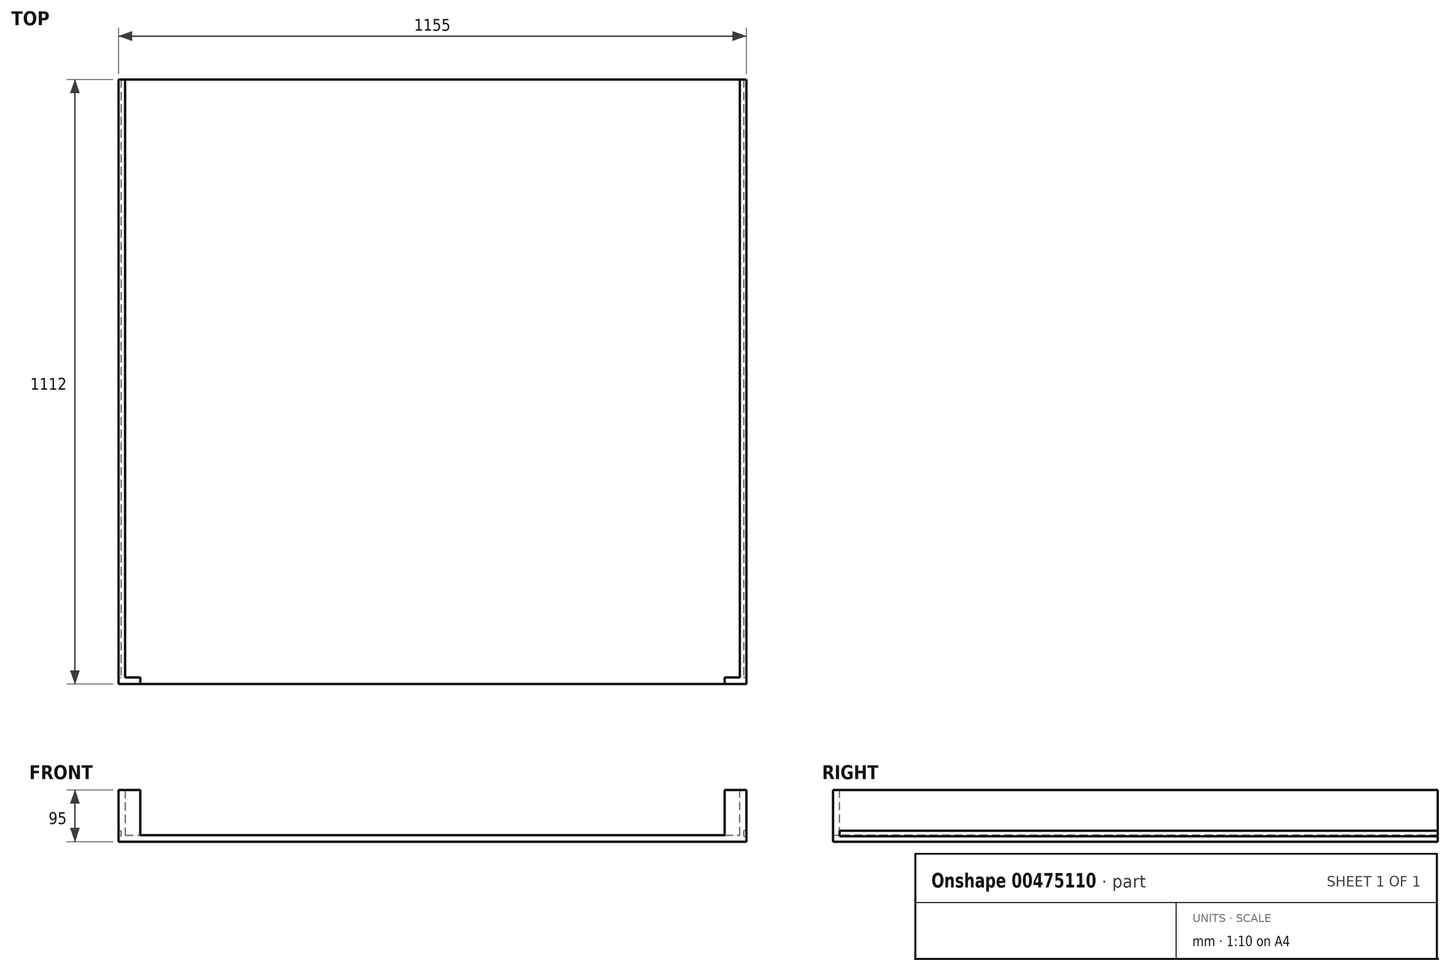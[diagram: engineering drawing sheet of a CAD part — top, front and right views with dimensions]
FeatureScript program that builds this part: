
annotation { "Feature Type Name" : "Feature", "Feature Type Description" : "" }
export const myFeature = defineFeature(function(context is Context, id is Id, definition is map)
    precondition{}
    {
        {
            var Q0;
            Q0=qCreatedBy(makeId("Front.planeOp"),FACE);
            var sketch = newSketch(context, id + "F0", { "sketchPlane" : qUnion([Q0])});
            skLineSegment(sketch, "E0.bottom", {"start": v(-577.5, 95) * mm, "end": v(577.5, 95) * mm, "construction": true});
            skLineSegment(sketch, "E0.top", {"start": v(-577.5, 0) * mm, "end": v(577.5, 0) * mm, "construction": true});
            skLineSegment(sketch, "E0.left", {"start": v(-577.5, 95) * mm, "end": v(-577.5, 0) * mm, "construction": true});
            skLineSegment(sketch, "E0.right", {"start": v(577.5, 95) * mm, "end": v(577.5, 0) * mm, "construction": true});
            skLineSegment(sketch, "E1", {"start": v(-577.5, 12) * mm, "end": v(577.5, 12) * mm, "construction": true});
            skLineSegment(sketch, "E2", {"start": v(-572.5, 95) * mm, "end": v(-572.5, 0) * mm, "construction": true});
            skLineSegment(sketch, "E3", {"start": v(572.5, 95) * mm, "end": v(572.5, 0) * mm, "construction": true});
            skLineSegment(sketch, "E4", {"start": v(565.5, 95) * mm, "end": v(565.5, 0) * mm, "construction": true});
            skLineSegment(sketch, "E5", {"start": v(-577.5, 10) * mm, "end": v(577.5, 10) * mm, "construction": true});
            skLineSegment(sketch, "E6", {"start": v(-577.5, 20) * mm, "end": v(577.5, 20) * mm, "construction": true});
            skLineSegment(sketch, "E7", {"start": v(-565.5, 12) * mm, "end": v(565.5, 12) * mm});
            skLineSegment(sketch, "E8", {"start": v(577.5, 0) * mm, "end": v(-577.5, 0) * mm});
            skLineSegment(sketch, "E9", {"start": v(-577.5, 95) * mm, "end": v(-577.5, 20) * mm});
            skLineSegment(sketch, "E10", {"start": v(-572.5, 20) * mm, "end": v(-572.5, 10) * mm});
            skLineSegment(sketch, "E11", {"start": v(-572.5, 10) * mm, "end": v(-577.5, 10) * mm});
            skLineSegment(sketch, "E12", {"start": v(-577.5, 20) * mm, "end": v(-572.5, 20) * mm});
            skLineSegment(sketch, "E13", {"start": v(-577.5, 10) * mm, "end": v(-577.5, 0) * mm});
            skLineSegment(sketch, "E14", {"start": v(-577.5, 95) * mm, "end": v(-565.5, 95) * mm});
            skLineSegment(sketch, "E15", {"start": v(565.5, 12) * mm, "end": v(565.5, 95) * mm});
            skLineSegment(sketch, "E16", {"start": v(565.5, 95) * mm, "end": v(577.5, 95) * mm});
            skLineSegment(sketch, "E17", {"start": v(577.5, 95) * mm, "end": v(577.5, 20) * mm});
            skLineSegment(sketch, "E18", {"start": v(577.5, 20) * mm, "end": v(572.5, 20) * mm});
            skLineSegment(sketch, "E19", {"start": v(572.5, 10) * mm, "end": v(577.5, 10) * mm});
            skLineSegment(sketch, "E20", {"start": v(572.5, 20) * mm, "end": v(572.5, 10) * mm});
            skLineSegment(sketch, "E21", {"start": v(577.5, 10) * mm, "end": v(577.5, 0) * mm});
            skLineSegment(sketch, "E22", {"start": v(-565.5, 0) * mm, "end": v(-565.5, 95) * mm, "construction": true});
            skLineSegment(sketch, "E23", {"start": v(-565.5, 95) * mm, "end": v(-565.5, 12) * mm});
            skSolve(sketch);
        }
        {
            var Q0;
            Q0=qSketchRegion(id+"F0",true);
            extrude(context, id + "F1", {"entities" : qUnion([Q0]), "oppositeDirection" : true, "depth" : 1100 * mm});
        }
        {
            var Q0;
            Q0=qCreatedBy(makeId("Front.planeOp"),FACE);
            var sketch = newSketch(context, id + "F2", { "sketchPlane" : qUnion([Q0])});
            skLineSegment(sketch, "E24.bottom", {"start": v(-577.5, 95) * mm, "end": v(577.5, 95) * mm, "construction": true});
            skLineSegment(sketch, "E24.top", {"start": v(-577.5, 0) * mm, "end": v(577.5, 0) * mm, "construction": true});
            skLineSegment(sketch, "E24.left", {"start": v(-577.5, 95) * mm, "end": v(-577.5, 0) * mm, "construction": true});
            skLineSegment(sketch, "E24.right", {"start": v(577.5, 95) * mm, "end": v(577.5, 0) * mm, "construction": true});
            skLineSegment(sketch, "E25", {"start": v(-537.5, 95) * mm, "end": v(-537.5, 0) * mm, "construction": true});
            skLineSegment(sketch, "E26", {"start": v(537.5, 95) * mm, "end": v(537.5, 0) * mm, "construction": true});
            skLineSegment(sketch, "E27", {"start": v(-577.5, 12) * mm, "end": v(577.5, 12) * mm, "construction": true});
            skLineSegment(sketch, "E28", {"start": v(-577.5, 95) * mm, "end": v(-537.5, 95) * mm});
            skLineSegment(sketch, "E29", {"start": v(-537.5, 95) * mm, "end": v(-537.5, 12) * mm});
            skLineSegment(sketch, "E30", {"start": v(-537.5, 12) * mm, "end": v(537.5, 12) * mm});
            skLineSegment(sketch, "E31", {"start": v(537.5, 12) * mm, "end": v(537.5, 95) * mm});
            skLineSegment(sketch, "E32", {"start": v(537.5, 95) * mm, "end": v(577.5, 95) * mm});
            skLineSegment(sketch, "E33", {"start": v(577.5, 95) * mm, "end": v(577.5, 0) * mm});
            skLineSegment(sketch, "E34", {"start": v(577.5, 0) * mm, "end": v(-577.5, 0) * mm});
            skLineSegment(sketch, "E35", {"start": v(-577.5, 0) * mm, "end": v(-577.5, 95) * mm});
            skSolve(sketch);
        }
        {
            var Q0;
            Q0=qSketchRegion(id+"F2",true);
            extrude(context, id + "F3", {"entities" : qUnion([Q0]), "operationType" : NewBodyOperationType.ADD, "depth" : 12 * mm});
        }
    });
